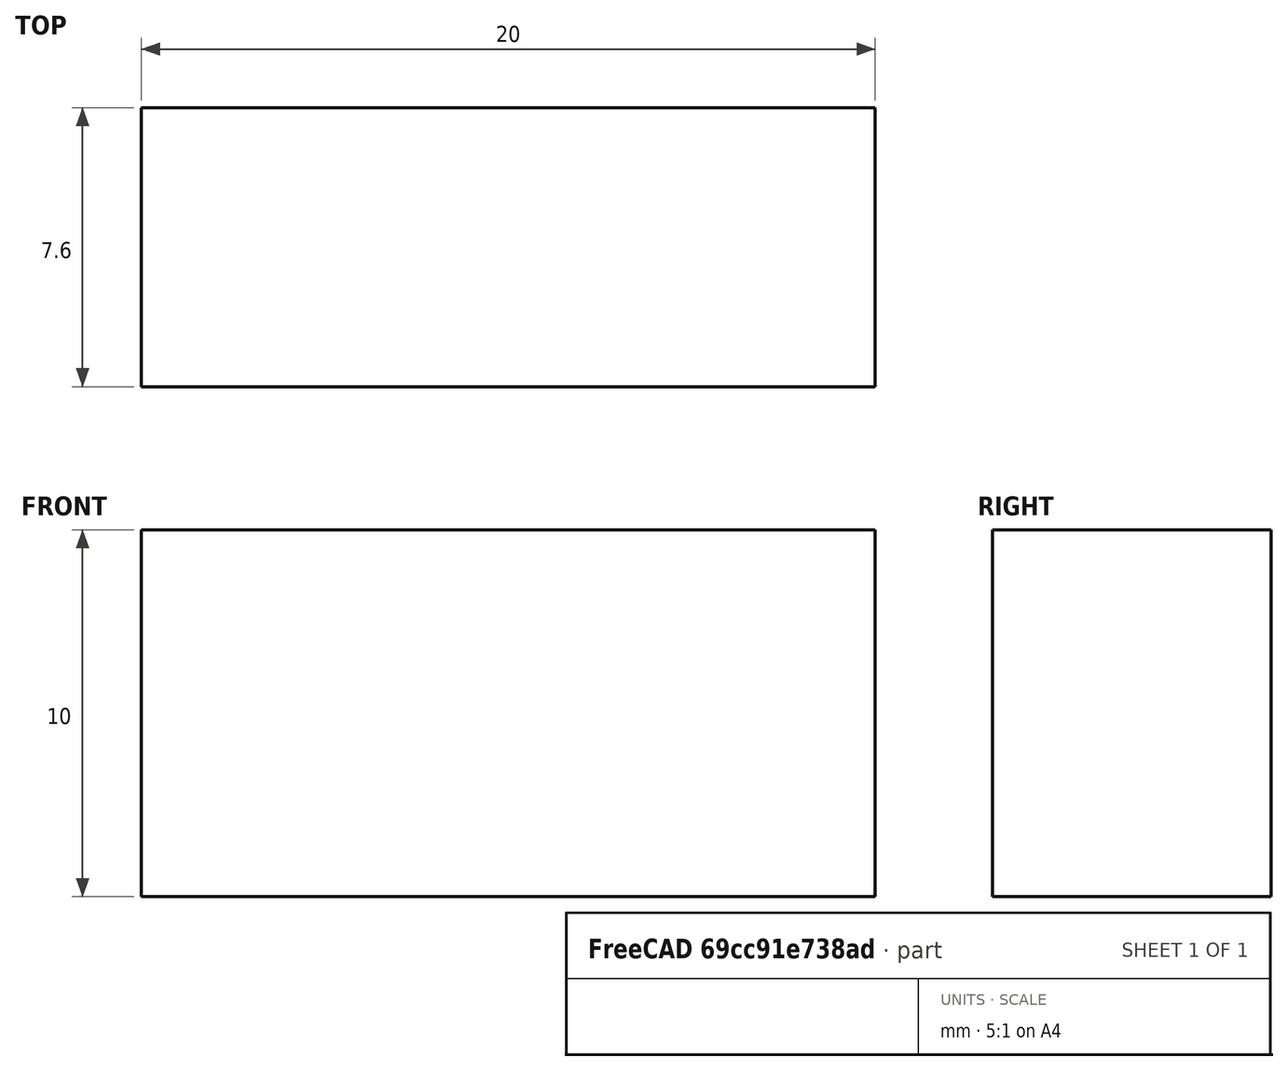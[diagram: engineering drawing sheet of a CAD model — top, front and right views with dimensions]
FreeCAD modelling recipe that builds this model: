
FCSTD DOCUMENT  (FreeCAD 2024.2R37179 (Git))
Label: Body
License: All rights reserved
LicenseURL: https://en.wikipedia.org/wiki/All_rights_reserved
objects: Sketcher::SketchObject×1, PartDesign::Pad×1, PartDesign::Body×1
note: 4 computed .brp shape members not serialized (recipe doc carries the construction recipe); baked Part::Feature solids carry a one-line shape summary decoded from their .brp

FEATURE [Sketcher::SketchObject] Sketch
  AttachmentSupport = -> [XY_Plane]
  FullyConstrained = true
  MapMode = 5
  sketch-geometry (4):
    g0: LineSegment StartX=0 StartY=0 StartZ=0 EndX=20 EndY=0 EndZ=0
    g1: LineSegment StartX=20 StartY=0 StartZ=0 EndX=20 EndY=7.6 EndZ=0
    g2: LineSegment StartX=20 StartY=7.6 StartZ=0 EndX=0 EndY=7.6 EndZ=0
    g3: LineSegment StartX=0 StartY=7.6 StartZ=0 EndX=0 EndY=0 EndZ=0
  constraints (11):
    c: Coincident(g0,g1)
    c: Coincident(g1,g2)
    c: Coincident(g2,g3)
    c: Coincident(g3,g0)
    c: Horizontal(g0)
    c: Horizontal(g2)
    c: Vertical(g1)
    c: Vertical(g3)
    c: Distance(g1,g3) = 20
    c: Distance(g0,g2) = 7.6
    c: Coincident(g0,g-1)
FEATURE [PartDesign::Pad] Pad
  Direction = (0,0,1)
  Length = 10
  Length2 = 10
  Profile = -> Sketch
  ReferenceAxis = -> Sketch [N_Axis]
  Refine = true
  Suppressed = false
  Type = 0
FEATURE [PartDesign::Body] Body
  Group = -> [Sketch,Pad]
  Origin = -> Origin
  Tip = -> Pad
